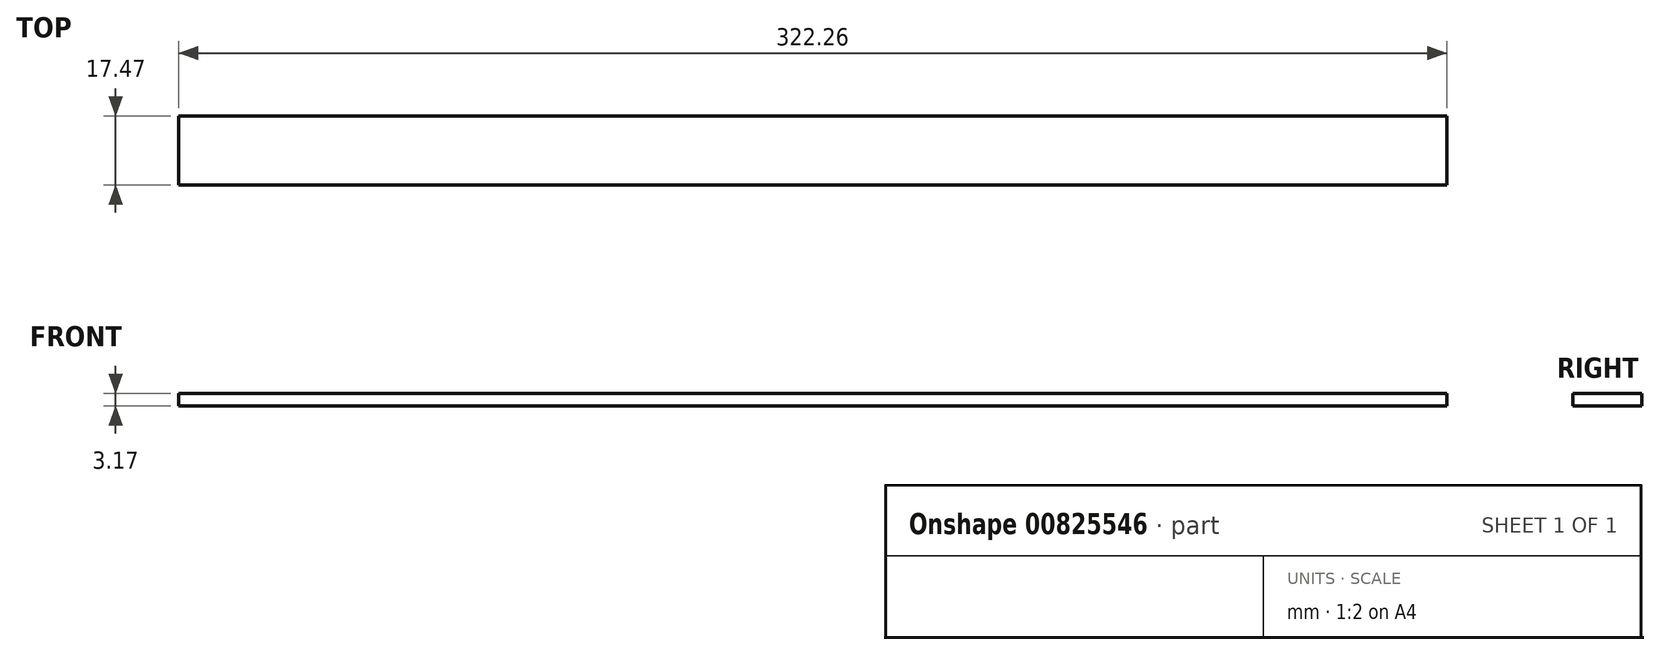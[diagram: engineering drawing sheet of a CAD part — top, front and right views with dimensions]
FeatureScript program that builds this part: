
annotation { "Feature Type Name" : "Feature", "Feature Type Description" : "" }
export const myFeature = defineFeature(function(context is Context, id is Id, definition is map)
    precondition{}
    {
        {
            var Q0;
            Q0=qCreatedBy(makeId("Top.planeOp"),FACE);
            var sketch = newSketch(context, id + "F0", { "sketchPlane" : qUnion([Q0])});
            skLineSegment(sketch, "E0.bottom", {"start": v(-161.13, -11.06) * mm, "end": v(161.13, -11.06) * mm});
            skLineSegment(sketch, "E0.top", {"start": v(-161.13, 6.4) * mm, "end": v(161.13, 6.4) * mm});
            skLineSegment(sketch, "E0.left", {"start": v(-161.13, -11.06) * mm, "end": v(-161.13, 6.4) * mm});
            skLineSegment(sketch, "E0.right", {"start": v(161.13, -11.06) * mm, "end": v(161.13, 6.4) * mm});
            skPoint(sketch, "E0.middle", {"position": v(0, -2.32) * mm});
            skSolve(sketch);
        }
        {
            var Q0;
            Q0=qSketchRegion(id+"F0",true);
            extrude(context, id + "F1", {"entities" : qUnion([Q0]), "depth" : 3.17 * mm, "offsetDistance" : 25.4 * mm});
        }
    });
